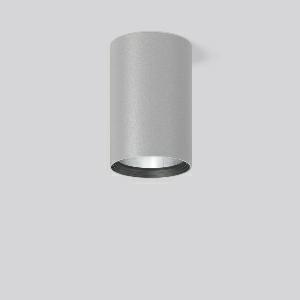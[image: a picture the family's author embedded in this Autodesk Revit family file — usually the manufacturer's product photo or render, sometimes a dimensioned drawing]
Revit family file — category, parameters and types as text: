
# Revit family: heledon_maxi_a_931225_004_1_aa3d
name_source: partatom
category: Lighting Fixtures
units: mm (PartAtom-declared; Revit-internal decimal feet)

## family parameters
Cut with Voids When Loaded = No
Host = Face
Light Source = No
Part Type = Normal
Room Calculation Point = No
Round Connector Dimension = Use Diameter
Shared = No

## types (1)
- HELEDON maxi A (1 x LED Modul 940, 4550 lm, 4000)
    Apparent Load = 35 VA
    Approval mark = CE
    CIE Flux Codes = 100 100 100 100 100
    Color Rendering = 92
    Color Temperature = 4000
    Default Elevation = 1800 mm
    Description = Series: HELEDON maxi
Cylindrical surface-mounted downlight. Housing: die-cast aluminium, powder-coated. Internal ceiling frame polycarbonate with bayonet mounting. Black plastic ring and recessed LED to prevent glare from the side. Optical assembly with reflector made of MIRO-Silver with 98% total light reflection for outstanding efficiency - can be changed without tools. Best colour rendering index Ra>90. Suitable for Ceiling mounting. Easy installation with a separate ceiling frame with bayonet mounting and plug connection. Driver integrated. Connected via plug-in connector. High quality converter without flickering and stroboscopic effect. The following accessories can be mounted without use of tools: interchangeable lenses, decorative glasses, honeycomb louvre, clear and frosted diffusers, white interchangeable plastic ring. 
Colour: silver
Diameter: 123 mm
Height: 183 mm
Lamp: LED
Socket: without socket
Colour temperature: 4000K
Colour rendering index (CRI): 92
System power: 35 W
Rated luminous flux: 4550 lm
Luminous efficiency: 130 lm/W
Control gear: Regulated power supply
Protection class: I
Type of protection: IP 20
    Height = 183 mm
    Lamp = 1 x LED Modul 940
    Lamp Light Flux = 4550 lm
    Lamp count = 1
    Length = 123 mm
    Lifetime = 50000 h
    Luminous efficacy = 130 lm/W
    Manufacturer = RZB
    ModVariant = No
    Model = 931225.004.1
    Mounting Place = Ceiling
    Mounting Type = Surface mounted
    Number of Poles = 1
    OnlyDefault = Yes
    Power Factor = 1
    Product Name = HELEDON maxi A
    Product group = Surface mounted downlights
    ProductGroupID = 302
    Protection Class = Protection class I
    Protection Degree = IP 20
    RLX_Detail_Level = 1
    RLX_Emergency_Light_Flux = 0 lm
    RLX_Emergency_Type = 0
    RLX_Emergency_Type_DB = No
    RlxData = <blob elided: 99997 chars, md5=ed2f9890>
    Socket = socket
    Standby Power = 0 W
    System Light Flux = 4550 lm
    System Power = 35 W
    Type Comments = Product without accessories
    Type Image = 931192.004.jpg
    URL = http://relux.com
    VarID = ---
    Voltage = 230 V
    Voltage Range = 220-240 V
    Weight = 0.00 kg
    Width = 0 mm  [stored 0 ft]

note: [stored X ft] marks values corroborated as IEEE doubles in the binary element streams (Revit-internal decimal feet)

## geometry (parser evidence)
native form markers: Blend x4, Sweep x11
no freeform markers — native parametric forms only
